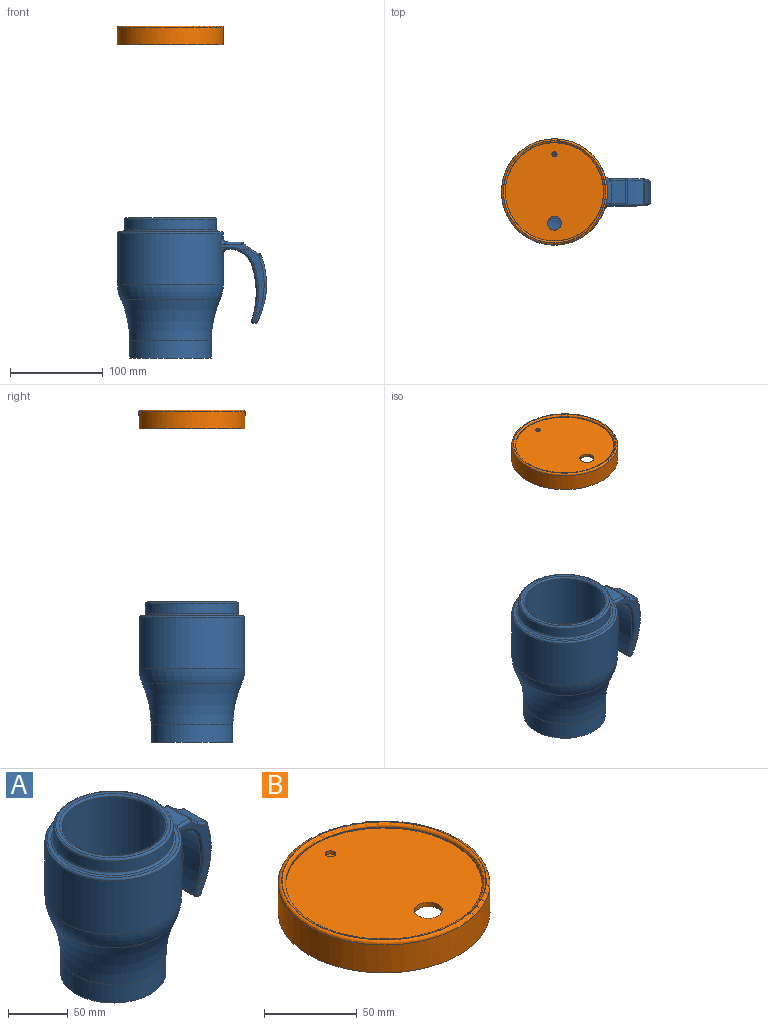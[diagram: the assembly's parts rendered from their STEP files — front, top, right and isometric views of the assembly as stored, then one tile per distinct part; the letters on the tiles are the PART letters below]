
ASSEMBLY  parts=2 mates=1
PART A: 67 faces, bbox 184.7x162.2x217.7 mm
  f0: cylinder r=92.44mm len=59.29mm, axis (0,-1,0), area 1226mm2, adj f32,f40,f44,f45
  f1: plane 17.27x1.65mm, normal (0,0,-1), area 28.5mm2, adj f30,f39,f44,f47
  f2: cylinder r=87.9mm len=72.64mm, axis (0,-1,0), area 1559.8mm2, adj f28,f30,f31,f61
  f3: plane 88x88mm, normal (0,0,-1), area 6082.1mm2, adj f4
  f4: cylinder r=44mm len=88mm, axis (0,0,1), area 5236.1mm2, adj f3,f5
  f5: torus R=150.55mm, axis (0,0,1), area 13470.7mm2, adj f4,f6
  f6: torus R=18.31mm, axis (0,0,1), area 5787.2mm2, adj f5,f7
  f7: cylinder r=57mm len=114mm, axis (0,0,1), area 19070.3mm2, adj f6,f8,f33,f49,f50,f51,f52,f53
  f8: torus R=55mm, axis (0,0,1), area 1110.8mm2, adj f7,f9
  f9: plane 110x110mm, normal (0,0,1), area 1008.5mm2, adj f8,f10
  f10: torus R=52mm, axis (0,0,1), area 1001.3mm2, adj f9,f11
  f11: cylinder r=50mm len=100mm, axis (0,0,1), area 3455.8mm2, adj f10,f12
  f12: torus R=48mm, axis (0,0,1), area 972.6mm2, adj f11,f13
  f13: plane 96x96mm, normal (0,0,1), area 876.5mm2, adj f12,f14
  f14: torus R=45mm, axis (0,0,1), area 863.1mm2, adj f13,f15
  f15: cylinder r=43mm len=86mm, axis (0,0,1), area 18912.4mm2, adj f14,f16
  f16: torus R=18.31mm, axis (0,0,1), area 2795mm2, adj f15,f17
  f17: torus R=150.55mm, axis (0,0,1), area 10855.7mm2, adj f16,f18
  f18: cylinder r=30mm len=60mm, axis (0,0,1), area 554.1mm2, adj f17,f19
  f19: torus R=28mm, axis (0,0,1), area 577.8mm2, adj f18,f20
  f20: plane 56x56mm, normal (0,0,1), area 2463mm2, adj f19
  f21: plane 25x16.12mm, normal (0,0,1), area 381.7mm2, adj f27,f29,f52,f62
  f22: plane 24.83x5.52mm, normal (0,-1,0), area 85.9mm2, adj f25,f27,f38,f41,f54,f57,f58
  f23: plane 25x3.31mm, normal (0,0,-1), area 61.6mm2, adj f32,f33,f34,f38
  f24: plane 24.83x5.52mm, normal (0,1,0), area 85.9mm2, adj f26,f29,f34,f36,f50,f65,f66
  f25: plane 77.44x25.78mm, normal (0,-1,-0.05), area 476.4mm2, adj f22,f28,f41,f43,f45,f47,f57
  f26: plane 77.44x25.78mm, normal (0,1,-0.05), area 476.4mm2, adj f24,f31,f36,f37,f39,f40,f65
  f27: cylinder r=2.5mm len=18.63mm, axis (1,0,0), area 68.2mm2, adj f21,f22,f53,f60
  f28: bspline ~73.1x12.22mm, area 292.3mm2, adj f2,f25,f48,f59
  f29: cylinder r=2.5mm len=18.63mm, axis (-1,0,0), area 68.2mm2, adj f21,f24,f51,f64
  f30: cylinder r=2.5mm len=17.27mm, axis (0,-1,0), area 47mm2, adj f1,f2,f35,f48
  f31: bspline ~73.1x12.22mm, area 292.3mm2, adj f2,f26,f35,f63
  f32: cylinder r=25mm len=25mm, axis (0,-1,0), area 765.4mm2, adj f0,f23,f36,f37,f41,f43
  f33: torus R=62mm, axis (0,0,-1), area 187.6mm2, adj f7,f23,f49,f55
  f34: cylinder r=2.5mm len=5.36mm, axis (-1,0,0), area 17mm2, adj f23,f24,f36,f49
  f35: sphere r=2.5mm, area 6.5mm2, adj f30,f31,f39
  f36: torus R=27.5mm, axis (0,-1,0), area 43.2mm2, adj f24,f26,f32,f34,f37
  f37: bspline ~17.11x15.84mm, area 82.6mm2, adj f26,f32,f36,f40
  f38: cylinder r=2.5mm len=5.36mm, axis (1,0,0), area 17mm2, adj f22,f23,f41,f55
  f39: cylinder r=2.5mm len=2.5mm, axis (1,0,0), area 6.3mm2, adj f1,f26,f35,f42
  f40: bspline ~60.9x7.61mm, area 239.7mm2, adj f0,f26,f37,f42
  f41: torus R=27.5mm, axis (0,-1,0), area 43.2mm2, adj f22,f25,f32,f38,f43
  f42: sphere r=2.5mm, area 19.5mm2, adj f39,f40,f44
  f43: bspline ~17.11x15.84mm, area 82.6mm2, adj f25,f32,f41,f45
  f44: cylinder r=2.5mm len=17.27mm, axis (0,-1,0), area 82.2mm2, adj f0,f1,f42,f46
  f45: bspline ~60.9x7.61mm, area 239.7mm2, adj f0,f25,f43,f46
  f46: sphere r=2.5mm, area 6.3mm2, adj f44,f45,f47
  f47: cylinder r=2.5mm len=2.5mm, axis (-1,0,0), area 6.3mm2, adj f1,f25,f46,f48
  f48: sphere r=2.5mm, area 6.5mm2, adj f28,f30,f47
  f49: bspline ~9.12x7.4mm, area 48.5mm2, adj f7,f33,f34,f50
  f50: cylinder r=5mm len=4.73mm, axis (0,0,1), area 18.6mm2, adj f7,f24,f49,f51
  f51: bspline ~9.11x7.28mm, area 48.5mm2, adj f7,f29,f50,f52
  f52: torus R=62mm, axis (0,0,1), area 187.6mm2, adj f7,f21,f51,f53
  f53: bspline ~9.11x8.43mm, area 48.5mm2, adj f7,f27,f52,f54
  f54: cylinder r=5mm len=4.73mm, axis (0,0,1), area 18.6mm2, adj f7,f22,f53,f55
  f55: bspline ~9.03x8.44mm, area 48.5mm2, adj f7,f33,f38,f54
  f56: cylinder r=45.74mm len=26mm, axis (0,-1,0), area 564.5mm2, adj f57,f58,f59,f60,f61,f62,f63,f64
  f57: bspline ~12.38x8.08mm, area 41.7mm2, adj f22,f25,f56,f58,f59
  f58: torus R=47.74mm, axis (0,-1,0), area 25.2mm2, adj f22,f56,f57,f60
  f59: bspline ~3.14x2.66mm, area 5.7mm2, adj f28,f56,f57,f61
  f60: bspline ~2.69x2.64mm, area 5.4mm2, adj f27,f56,f58,f62
  f61: cylinder r=2mm len=24.32mm, axis (0,-1,0), area 41.5mm2, adj f2,f56,f59,f63
  f62: cylinder r=2mm len=25mm, axis (0,-1,0), area 41.3mm2, adj f21,f56,f60,f64
  f63: bspline ~3.39x3.13mm, area 5.7mm2, adj f31,f56,f61,f65
  f64: bspline ~3.31x3.25mm, area 5.4mm2, adj f29,f56,f62,f66
  f65: bspline ~12.38x8.08mm, area 41.7mm2, adj f24,f26,f56,f63,f66
  f66: torus R=47.74mm, axis (0,-1,0), area 25.2mm2, adj f24,f56,f64,f65
PART B: 14 faces, bbox 123.7x123.7x20.4 mm
  f0: plane 114.27x114.27mm, normal (0,0,-1), area 1760.3mm2, adj f1,f8
  f1: cylinder r=57.13mm len=114.27mm, axis (0,0,-1), area 6621.6mm2, adj f0,f11
  f2: plane 110.27x110.27mm, normal (0,0,1), area 61.2mm2, adj f11,f12
  f3: cylinder r=52.96mm len=105.91mm, axis (0,0,-1), area 195.4mm2, adj f4,f12
  f4: plane 105.91x105.91mm, normal (0,0,1), area 8610.1mm2, adj f3,f10,f13
  f5: plane 96x96mm, normal (0,0,-1), area 7056mm2, adj f6,f9,f13
  f6: torus R=48mm, axis (0,0,-1), area 972.6mm2, adj f5,f7
  f7: cylinder r=50mm len=100mm, axis (0,0,-1), area 3455.8mm2, adj f6,f8
  f8: torus R=52mm, axis (0,0,-1), area 1001.3mm2, adj f0,f7
  f9: cone r=0mm half-angle=59deg, axis (0,0,1), area 21.3mm2, adj f5,f10
  f10: cylinder r=2.75mm len=5.5mm, axis (0,0,1), area 34.6mm2, adj f4,f9
  f11: torus R=55.13mm, axis (0,0,1), area 1113.4mm2, adj f1,f2
  f12: torus R=54.96mm, axis (0,0,1), area 1059.7mm2, adj f2,f3
  f13: cylinder r=7.5mm len=15mm, axis (0,0,1), area 134.7mm2, adj f4,f5
PLACE A at identity fixed
PLACE B t=(0,0,201.41)mm
MATE slider A.f4 <-> B.f1  axis (0,0,1) through (0,0,136)mm
